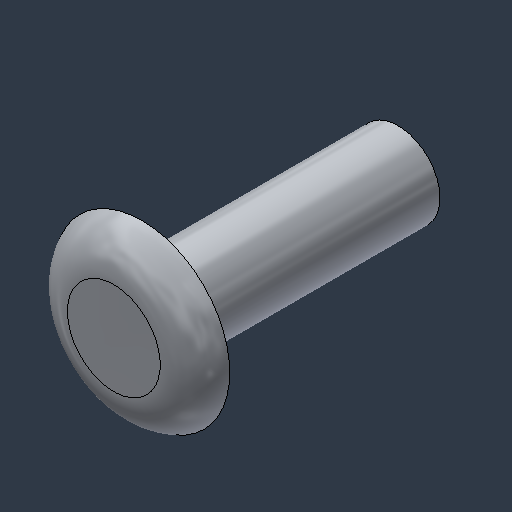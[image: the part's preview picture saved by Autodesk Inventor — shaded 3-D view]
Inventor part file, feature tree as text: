
AUTODESK INVENTOR PART (.ipt)
format: ipt  version: 2024.3 (Build 283343000, 343)  size: 123,392 bytes
history: native  units: mm (DEFAULTED — no unit token found)
features: fillet x1
ambient origin geometry x8: Origin, YZ Plane, XZ Plane, XY Plane, X Axis, Y Axis, Z Axis, Center Point
bodies: Solid1 (feature_tree)
feature tree (1):
  fillet  "Fillet1"  [1 undecoded]
note: 1 required parameter value undecoded (feature->parameter linkage not recoverable at this tier; creation-order binding heuristic only, values carry confidence <= 0.55)
